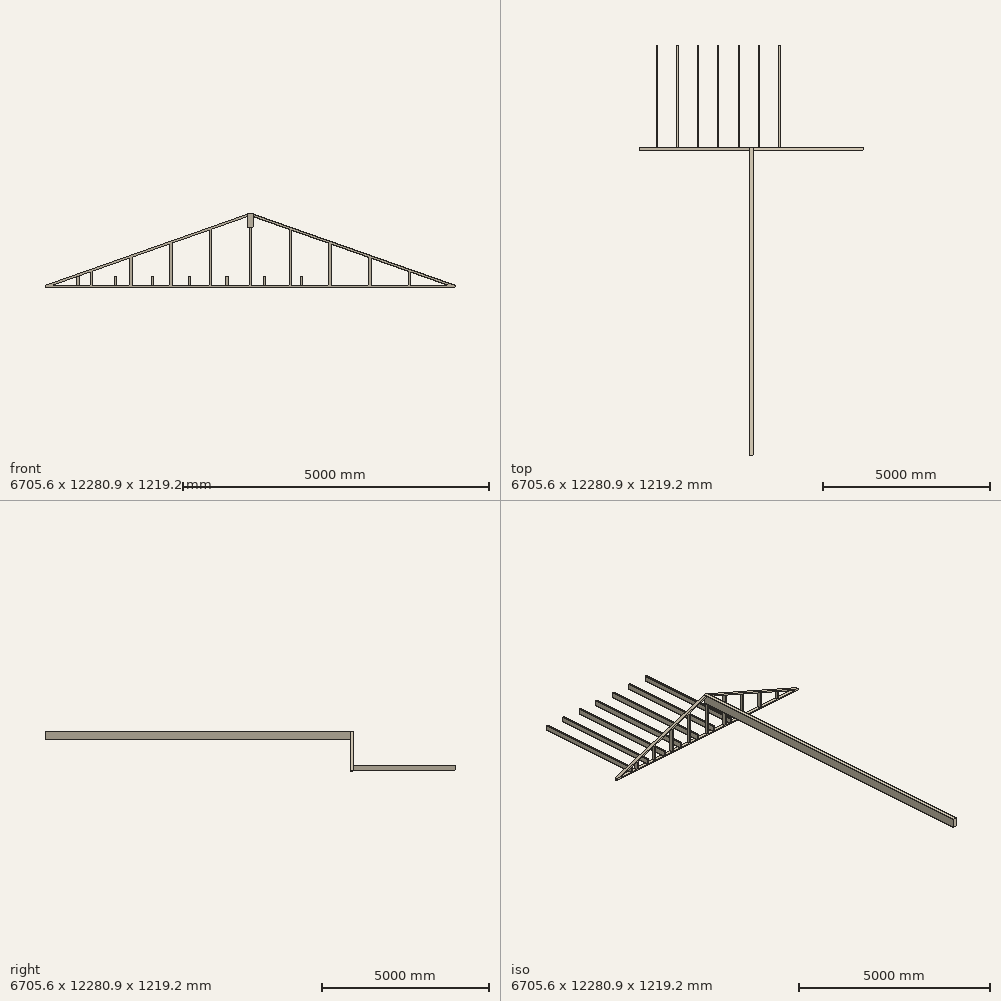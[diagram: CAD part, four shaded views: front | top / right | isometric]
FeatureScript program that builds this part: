
annotation { "Feature Type Name" : "Feature", "Feature Type Description" : "" }
export const myFeature = defineFeature(function(context is Context, id is Id, definition is map)
    precondition{}
    {
        {
            assignVariable(context, id + "F0", {"name" : "FourBy", "anyValue" : 88.9 * mm});
        }
        {
            var Q0;
            Q0=qCreatedBy(makeId("Front.planeOp"),FACE);
            var sketch = newSketch(context, id + "F1", { "sketchPlane" : qUnion([Q0])});
            skLineSegment(sketch, "E0.bottom", {"start": v(-3238.13, 38.1) * mm, "end": v(-2624.8, 38.1) * mm});
            skLineSegment(sketch, "E0.top", {"start": v(-3352.8, 0) * mm, "end": v(0, 0) * mm});
            skLineSegment(sketch, "E0.left", {"start": v(-3352.8, 38.1) * mm, "end": v(-3352.8, 0) * mm});
            skLineSegment(sketch, "E1", {"start": v(-3352.8, 38.1) * mm, "end": v(-57.15, 1199.07) * mm});
            skLineSegment(sketch, "E2", {"start": v(-57.15, 1158.67) * mm, "end": v(-632.39, 956.03) * mm});
            skLineSegment(sketch, "E3", {"start": v(-1321.92, 713.13) * mm, "end": v(-1321.92, 38.1) * mm});
            skLineSegment(sketch, "E4", {"start": v(-1283.82, 726.55) * mm, "end": v(-1283.82, 38.1) * mm});
            skLineSegment(sketch, "E5", {"start": v(-670.49, 942.61) * mm, "end": v(-670.49, 38.1) * mm});
            skLineSegment(sketch, "E6", {"start": v(-632.39, 956.03) * mm, "end": v(-632.39, 38.1) * mm});
            skLineSegment(sketch, "E7", {"start": v(-57.15, 1219.2) * mm, "end": v(-57.15, 1199.07) * mm});
            skLineSegment(sketch, "E8", {"start": v(-57.15, 977.9) * mm, "end": v(-19.05, 977.9) * mm});
            skLineSegment(sketch, "E9", {"start": v(0, 0) * mm, "end": v(0, 1219.2) * mm});
            skLineSegment(sketch, "E10", {"start": v(0, 1219.2) * mm, "end": v(-57.15, 1219.2) * mm});
            skLineSegment(sketch, "E11", {"start": v(-1973.36, 483.64) * mm, "end": v(-1973.36, 38.1) * mm});
            skLineSegment(sketch, "E12", {"start": v(-1935.26, 497.07) * mm, "end": v(-1935.26, 38.1) * mm});
            skLineSegment(sketch, "E13", {"start": v(-2624.8, 254.16) * mm, "end": v(-2624.8, 38.1) * mm});
            skLineSegment(sketch, "E14", {"start": v(-2586.7, 267.58) * mm, "end": v(-2586.7, 38.1) * mm});
            skLineSegment(sketch, "E15.right", {"start": v(-19.05, 977.9) * mm, "end": v(-19.05, 38.1) * mm});
            skLineSegment(sketch, "E16.trimOffspring", {"start": v(-2624.8, 254.16) * mm, "end": v(-3238.13, 38.1) * mm});
            skLineSegment(sketch, "E17.trimOffspring", {"start": v(-2586.7, 38.1) * mm, "end": v(-1973.36, 38.1) * mm});
            skLineSegment(sketch, "E18.trimOffspring", {"start": v(-1935.26, 38.1) * mm, "end": v(-1321.92, 38.1) * mm});
            skLineSegment(sketch, "E19.trimOffspring", {"start": v(-1973.36, 483.64) * mm, "end": v(-2586.7, 267.58) * mm});
            skLineSegment(sketch, "E20.trimOffspring", {"start": v(-1321.92, 713.13) * mm, "end": v(-1935.26, 497.07) * mm});
            skLineSegment(sketch, "E21.trimOffspring", {"start": v(-1283.82, 38.1) * mm, "end": v(-670.49, 38.1) * mm});
            skLineSegment(sketch, "E22.trimOffspring", {"start": v(-632.39, 38.1) * mm, "end": v(-19.05, 38.1) * mm});
            skLineSegment(sketch, "E23.trimOffspring", {"start": v(-670.49, 942.61) * mm, "end": v(-1283.82, 726.55) * mm});
            skLineSegment(sketch, "E24.trimOffspring", {"start": v(-57.15, 1158.67) * mm, "end": v(-57.15, 977.9) * mm});
            skLineSegment(sketch, "E25.MirrorCS", {"start": v(57.15, 1219.2) * mm, "end": v(57.15, 1199.07) * mm});
            skLineSegment(sketch, "E26.MirrorCS", {"start": v(3352.8, 38.1) * mm, "end": v(3352.8, 0) * mm});
            skLineSegment(sketch, "E27.MirrorCS", {"start": v(57.15, 977.9) * mm, "end": v(19.05, 977.9) * mm});
            skLineSegment(sketch, "E28.MirrorCS", {"start": v(0, 1219.2) * mm, "end": v(57.15, 1219.2) * mm});
            skLineSegment(sketch, "E29.MirrorCS", {"start": v(1935.26, 38.1) * mm, "end": v(1321.92, 38.1) * mm});
            skLineSegment(sketch, "E30.MirrorCS", {"start": v(1321.92, 713.13) * mm, "end": v(1935.26, 497.07) * mm});
            skLineSegment(sketch, "E31.MirrorCS", {"start": v(1283.82, 38.1) * mm, "end": v(670.49, 38.1) * mm});
            skLineSegment(sketch, "E32.MirrorCS", {"start": v(1935.26, 497.07) * mm, "end": v(1935.26, 38.1) * mm});
            skLineSegment(sketch, "E33.MirrorCS", {"start": v(19.05, 977.9) * mm, "end": v(19.05, 38.1) * mm});
            skLineSegment(sketch, "E34.MirrorCS", {"start": v(57.15, 1158.67) * mm, "end": v(57.15, 977.9) * mm});
            skLineSegment(sketch, "E35.MirrorCS", {"start": v(2624.8, 254.16) * mm, "end": v(2624.8, 38.1) * mm});
            skLineSegment(sketch, "E36.MirrorCS", {"start": v(2586.7, 267.58) * mm, "end": v(2586.7, 38.1) * mm});
            skLineSegment(sketch, "E37.MirrorCS", {"start": v(3352.8, 38.1) * mm, "end": v(57.15, 1199.07) * mm});
            skLineSegment(sketch, "E38.MirrorCS", {"start": v(3352.8, 0) * mm, "end": v(0, 0) * mm});
            skLineSegment(sketch, "E39.MirrorCS", {"start": v(2624.8, 254.16) * mm, "end": v(3238.13, 38.1) * mm});
            skLineSegment(sketch, "E40.MirrorCS", {"start": v(3238.13, 38.1) * mm, "end": v(2624.8, 38.1) * mm});
            skLineSegment(sketch, "E41.MirrorCS", {"start": v(57.15, 1158.67) * mm, "end": v(632.39, 956.03) * mm});
            skLineSegment(sketch, "E42.MirrorCS", {"start": v(1321.92, 713.13) * mm, "end": v(1321.92, 38.1) * mm});
            skLineSegment(sketch, "E43.MirrorCS", {"start": v(1973.36, 483.64) * mm, "end": v(2586.7, 267.58) * mm});
            skLineSegment(sketch, "E44.MirrorCS", {"start": v(632.39, 38.1) * mm, "end": v(19.05, 38.1) * mm});
            skLineSegment(sketch, "E45.MirrorCS", {"start": v(1283.82, 726.55) * mm, "end": v(1283.82, 38.1) * mm});
            skLineSegment(sketch, "E46.MirrorCS", {"start": v(1973.36, 483.64) * mm, "end": v(1973.36, 38.1) * mm});
            skLineSegment(sketch, "E47.MirrorCS", {"start": v(670.49, 942.61) * mm, "end": v(670.49, 38.1) * mm});
            skLineSegment(sketch, "E48.MirrorCS", {"start": v(632.39, 956.03) * mm, "end": v(632.39, 38.1) * mm});
            skLineSegment(sketch, "E49.MirrorCS", {"start": v(2586.7, 38.1) * mm, "end": v(1973.36, 38.1) * mm});
            skLineSegment(sketch, "E50.MirrorCS", {"start": v(670.49, 942.61) * mm, "end": v(1283.82, 726.55) * mm});
            skSolve(sketch);
        }
        {
            var Q0;
            Q0 = qSketchRegion(id + "F1", true);
            extrude(context, id + "F2", {"entities" : qUnion([Q0]), "depth" : getVariable(context, 'FourBy'), "offsetDistance" : 30.48 * mm});
        }
        {
            var Q0;
            Q0=qCreatedBy(makeId("Front.planeOp"),FACE);
            var sketch = newSketch(context, id + "F3", { "sketchPlane" : qUnion([Q0])});
            skLineSegment(sketch, "E51.0", {"start": v(-3238.13, 38.1) * mm, "end": v(-2624.8, 38.1) * mm, "construction": true});
            skLineSegment(sketch, "E51.1", {"start": v(-2586.7, 38.1) * mm, "end": v(-1973.36, 38.1) * mm, "construction": true});
            skLineSegment(sketch, "E51.2", {"start": v(-1935.26, 38.1) * mm, "end": v(-1321.92, 38.1) * mm, "construction": true});
            skLineSegment(sketch, "E51.3", {"start": v(-1283.82, 38.1) * mm, "end": v(-670.49, 38.1) * mm, "construction": true});
            skLineSegment(sketch, "E51.4", {"start": v(-632.39, 38.1) * mm, "end": v(-19.05, 38.1) * mm, "construction": true});
            skLineSegment(sketch, "E52.bottom", {"start": v(-2841.56, 177.8) * mm, "end": v(-2803.46, 177.8) * mm});
            skLineSegment(sketch, "E52.top", {"start": v(-2841.56, 38.1) * mm, "end": v(-2803.46, 38.1) * mm});
            skLineSegment(sketch, "E52.left", {"start": v(-2841.56, 177.8) * mm, "end": v(-2841.56, 38.1) * mm});
            skLineSegment(sketch, "E52.right", {"start": v(-2803.46, 177.8) * mm, "end": v(-2803.46, 38.1) * mm});
            skLineSegment(sketch, "E53.0", {"start": v(-2624.8, 254.16) * mm, "end": v(-3238.13, 38.1) * mm, "construction": true});
            skLineSegment(sketch, "E54.1.0.0", {"start": v(-2231.96, 177.8) * mm, "end": v(-2231.96, 38.1) * mm});
            skLineSegment(sketch, "E54.1.0.1", {"start": v(-2231.96, 177.8) * mm, "end": v(-2193.86, 177.8) * mm});
            skLineSegment(sketch, "E54.1.0.2", {"start": v(-2193.86, 177.8) * mm, "end": v(-2193.86, 38.1) * mm});
            skLineSegment(sketch, "E54.1.0.3", {"start": v(-2231.96, 38.1) * mm, "end": v(-2193.86, 38.1) * mm});
            skLineSegment(sketch, "E54.2.0.0", {"start": v(-1622.36, 177.8) * mm, "end": v(-1622.36, 38.1) * mm});
            skLineSegment(sketch, "E54.2.0.1", {"start": v(-1622.36, 177.8) * mm, "end": v(-1584.26, 177.8) * mm});
            skLineSegment(sketch, "E54.2.0.2", {"start": v(-1584.26, 177.8) * mm, "end": v(-1584.26, 38.1) * mm});
            skLineSegment(sketch, "E54.2.0.3", {"start": v(-1622.36, 38.1) * mm, "end": v(-1584.26, 38.1) * mm});
            skLineSegment(sketch, "E54.3.0.0", {"start": v(-1012.76, 177.8) * mm, "end": v(-1012.76, 38.1) * mm});
            skLineSegment(sketch, "E54.3.0.1", {"start": v(-1012.76, 177.8) * mm, "end": v(-974.66, 177.8) * mm});
            skLineSegment(sketch, "E54.3.0.2", {"start": v(-974.66, 177.8) * mm, "end": v(-974.66, 38.1) * mm});
            skLineSegment(sketch, "E54.3.0.3", {"start": v(-1012.76, 38.1) * mm, "end": v(-974.66, 38.1) * mm});
            skLineSegment(sketch, "E54.4.0.0", {"start": v(-403.16, 177.8) * mm, "end": v(-403.16, 38.1) * mm});
            skLineSegment(sketch, "E54.4.0.1", {"start": v(-403.16, 177.8) * mm, "end": v(-365.06, 177.8) * mm});
            skLineSegment(sketch, "E54.4.0.2", {"start": v(-365.06, 177.8) * mm, "end": v(-365.06, 38.1) * mm});
            skLineSegment(sketch, "E54.4.0.3", {"start": v(-403.16, 38.1) * mm, "end": v(-365.06, 38.1) * mm});
            skLineSegment(sketch, "E54.direction1", {"start": v(-2841.56, 38.1) * mm, "end": v(-2231.96, 38.1) * mm, "construction": true});
            skLineSegment(sketch, "E55.0.5.0", {"start": v(206.44, 177.8) * mm, "end": v(206.44, 38.1) * mm});
            skLineSegment(sketch, "E55.3.5.0", {"start": v(206.44, 177.8) * mm, "end": v(244.54, 177.8) * mm});
            skLineSegment(sketch, "E55.6.5.0", {"start": v(244.54, 177.8) * mm, "end": v(244.54, 38.1) * mm});
            skLineSegment(sketch, "E55.9.5.0", {"start": v(206.44, 38.1) * mm, "end": v(244.54, 38.1) * mm});
            skLineSegment(sketch, "E55.0.6.0", {"start": v(816.04, 177.8) * mm, "end": v(816.04, 38.1) * mm});
            skLineSegment(sketch, "E55.3.6.0", {"start": v(816.04, 177.8) * mm, "end": v(854.14, 177.8) * mm});
            skLineSegment(sketch, "E55.6.6.0", {"start": v(854.14, 177.8) * mm, "end": v(854.14, 38.1) * mm});
            skLineSegment(sketch, "E55.9.6.0", {"start": v(816.04, 38.1) * mm, "end": v(854.14, 38.1) * mm});
            skSolve(sketch);
        }
        {
            var Q0;
            Q0 = qSketchRegion(id + "F3", true);
            extrude(context, id + "F4", {"entities" : qUnion([Q0]), "depth" : getVariable(context, 'FourBy'), "offsetDistance" : 30.48 * mm, "hasSecondDirection" : true, "secondDirectionOppositeDirection" : true, "secondDirectionDepth" : 3048 * mm});
        }
        {
            var Q0;
            Q0=makeQuery(id+"F2.opExtrude","CAP_FACE",FACE,{"disambiguationData":[OSD([sQuery(id+"F1.wireOp",EDGE,"E0.bottom"),sQuery(id+"F1.wireOp",EDGE,"E0.top"),sQuery(id+"F1.wireOp",EDGE,"E0.left"),sQuery(id+"F1.wireOp",EDGE,"E1"),sQuery(id+"F1.wireOp",EDGE,"E2"),sQuery(id+"F1.wireOp",EDGE,"E3"),sQuery(id+"F1.wireOp",EDGE,"E4"),sQuery(id+"F1.wireOp",EDGE,"E5"),sQuery(id+"F1.wireOp",EDGE,"E6"),sQuery(id+"F1.wireOp",EDGE,"E7"),sQuery(id+"F1.wireOp",EDGE,"E8"),sQuery(id+"F1.wireOp",EDGE,"E10"),sQuery(id+"F1.wireOp",EDGE,"E11"),sQuery(id+"F1.wireOp",EDGE,"E12"),sQuery(id+"F1.wireOp",EDGE,"E13"),sQuery(id+"F1.wireOp",EDGE,"E14"),sQuery(id+"F1.wireOp",EDGE,"E15.right"),sQuery(id+"F1.wireOp",EDGE,"E16.trimOffspring"),sQuery(id+"F1.wireOp",EDGE,"E17.trimOffspring"),sQuery(id+"F1.wireOp",EDGE,"E18.trimOffspring"),sQuery(id+"F1.wireOp",EDGE,"E19.trimOffspring"),sQuery(id+"F1.wireOp",EDGE,"E20.trimOffspring"),sQuery(id+"F1.wireOp",EDGE,"E21.trimOffspring"),sQuery(id+"F1.wireOp",EDGE,"E22.trimOffspring"),sQuery(id+"F1.wireOp",EDGE,"E23.trimOffspring"),sQuery(id+"F1.wireOp",EDGE,"E24.trimOffspring"),sQuery(id+"F1.wireOp",EDGE,"E25.MirrorCS"),sQuery(id+"F1.wireOp",EDGE,"E26.MirrorCS"),sQuery(id+"F1.wireOp",EDGE,"E27.MirrorCS"),sQuery(id+"F1.wireOp",EDGE,"E28.MirrorCS"),sQuery(id+"F1.wireOp",EDGE,"E29.MirrorCS"),sQuery(id+"F1.wireOp",EDGE,"E30.MirrorCS"),sQuery(id+"F1.wireOp",EDGE,"E31.MirrorCS"),sQuery(id+"F1.wireOp",EDGE,"E32.MirrorCS"),sQuery(id+"F1.wireOp",EDGE,"E33.MirrorCS"),sQuery(id+"F1.wireOp",EDGE,"E34.MirrorCS"),sQuery(id+"F1.wireOp",EDGE,"E35.MirrorCS"),sQuery(id+"F1.wireOp",EDGE,"E36.MirrorCS"),sQuery(id+"F1.wireOp",EDGE,"E37.MirrorCS"),sQuery(id+"F1.wireOp",EDGE,"E38.MirrorCS"),sQuery(id+"F1.wireOp",EDGE,"E39.MirrorCS"),sQuery(id+"F1.wireOp",EDGE,"E40.MirrorCS"),sQuery(id+"F1.wireOp",EDGE,"E41.MirrorCS"),sQuery(id+"F1.wireOp",EDGE,"E42.MirrorCS"),sQuery(id+"F1.wireOp",EDGE,"E43.MirrorCS"),sQuery(id+"F1.wireOp",EDGE,"E44.MirrorCS"),sQuery(id+"F1.wireOp",EDGE,"E45.MirrorCS"),sQuery(id+"F1.wireOp",EDGE,"E46.MirrorCS"),sQuery(id+"F1.wireOp",EDGE,"E47.MirrorCS"),sQuery(id+"F1.wireOp",EDGE,"E48.MirrorCS"),sQuery(id+"F1.wireOp",EDGE,"E49.MirrorCS"),sQuery(id+"F1.wireOp",EDGE,"E50.MirrorCS")])],"isStart":false});
            var sketch = newSketch(context, id + "F5", { "sketchPlane" : qUnion([Q0])});
            skPoint(sketch, "E56.0", {"position": v(-57.15, 1219.2) * mm});
            skPoint(sketch, "E56.1", {"position": v(57.15, 1219.2) * mm});
            skPoint(sketch, "E56.2", {"position": v(57.15, 977.9) * mm});
            skPoint(sketch, "E56.3", {"position": v(-57.15, 977.9) * mm});
            skLineSegment(sketch, "E57.bottom", {"start": v(-57.15, 1219.2) * mm, "end": v(57.15, 1219.2) * mm});
            skLineSegment(sketch, "E57.top", {"start": v(-57.15, 977.9) * mm, "end": v(57.15, 977.9) * mm});
            skLineSegment(sketch, "E57.left", {"start": v(-57.15, 1219.2) * mm, "end": v(-57.15, 977.9) * mm});
            skLineSegment(sketch, "E57.right", {"start": v(57.15, 1219.2) * mm, "end": v(57.15, 977.9) * mm});
            skSolve(sketch);
        }
        {
            var Q0;
            Q0 = qSketchRegion(id + "F5", true);
            extrude(context, id + "F6", {"entities" : qUnion([Q0]), "operationType" : NewBodyOperationType.ADD, "depth" : 9144 * mm, "offsetDistance" : 30.48 * mm});
        }
    });
